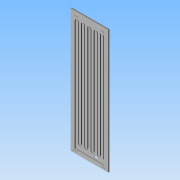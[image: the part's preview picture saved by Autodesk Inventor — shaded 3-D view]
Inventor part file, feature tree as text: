
AUTODESK INVENTOR PART (.ipt)
format: ipt  version: 2013 (Build 170138000, 138)  size: 271,360 bytes
history: native  units: in
note: dims shown in document units (in); Inventor stores cm internally (conversion verified against a paired STEP export)
features: other x12, extrude x3, hole x1
ambient origin geometry x8: Origin, YZ Plane, XZ Plane, XY Plane, X Axis, Y Axis, Z Axis, Center Point
bodies: Solid1 (feature_tree)
feature tree (16):
  other  "Blocks"
  extrude  "Stck Extrusion"  Depth=23.8125in
  extrude  "LED Extrusion3"  Depth=78.0in
  other  "Side profile reference"
  hole  "Hole1"  [1 undecoded]
  extrude  "Extrusion5"  Depth=66.0in
  other  "Stock"
  other  "LEDPocket"
  other  "TwoLineColumn"
  other  "TwoLineColumnEnd"
  other  "15mm Neon profile"
  other  "U Bolt hole and bore"
  other  "U-Bolt holes"
  other  "Through panel"
  other  "15mm Neon profile:1"
  other  "15mm Neon profile:2"
note: 1 required parameter value undecoded (feature->parameter linkage not recoverable at this tier; creation-order binding heuristic only, values carry confidence <= 0.55)
